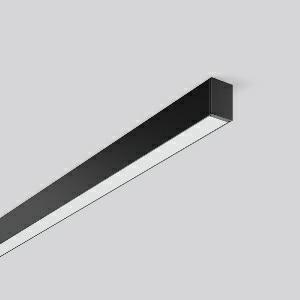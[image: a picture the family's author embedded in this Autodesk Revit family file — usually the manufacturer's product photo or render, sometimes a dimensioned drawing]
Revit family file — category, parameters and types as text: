
# Revit family: less_is_more_27_312198_003_1_fe82
name_source: partatom
category: Lighting Fixtures
units: mm (PartAtom-declared; Revit-internal decimal feet)

## family parameters
Cut with Voids When Loaded = No
Host = Face
Light Source = No
Part Type = Normal
Room Calculation Point = No
Round Connector Dimension = Use Diameter
Shared = No

## types (1)
- LESS IS MORE 27 (1 x LED Modul 840, 1900 lm, 4000)
    Apparent Load = 31 VA
    CIE Flux Codes = 48 79 96 100 100
    Color Rendering = 80
    Color Temperature = 4000
    Default Elevation = 1800 mm
    Description = Series: LESS IS MORE 27
Ceiling and wall luminaire with slim design. Housing: extruded aluminium profile, powder-coated. End cap aluminium powder-coated. Diffuser made of non-yellowing plastic (PMMA), opal. Suitable for Ceiling mounting, Wall (surface). External driver with connecting cable. 
Colour: deep black, matt (RAL 9005)
Length: 1212 mm
Width: 28 mm
Height: 38 mm
Lamp: LED
Socket: without socket
Colour temperature: 4000K
Colour rendering index (CRI): 82
System power: 31 W
Rated luminous flux: 1900 lm
Luminous efficiency: 61 lm/W
Control gear: Regulated power supply
Protection class: II
Type of protection: IP 20
    Height = 38 mm
    Lamp = 1 x LED Modul 840
    Lamp Light Flux = 1900 lm
    Lamp count = 1
    Length = 1212 mm
    Lifetime = 50000 h
    Luminous efficacy = 61 lm/W
    Manufacturer = RZB
    ModVariant = No
    Model = 312198.003.1
    Mounting Place = Ceiling, Wall
    Mounting Type = Surface mounted
    Number of Poles = 1
    OnlyDefault = Yes
    Power Factor = 1
    Product Name = LESS IS MORE 27
    Product group = Surface mounted LED linear luminaires
    ProductGroupID = 307
    Protection Class = Protection class II
    Protection Degree = IP 20
    RLX_Detail_Level = 1
    RLX_Emergency_Light_Flux = 0 lm
    RLX_Emergency_Type = 0
    RLX_Emergency_Type_DB = No
    RlxData = <blob elided: 28685 chars, md5=6dc0d3b8>
    Socket = socket
    Standby Power = 0 W
    System Light Flux = 1900 lm
    System Power = 31 W
    Type Comments = Product without accessories
    Type Image = 312196.003.jpg
    URL = http://relux.com
    VarID = ---
    Voltage = 230 V
    Voltage Range = 220-240 V
    Weight = 0.00 kg
    Width = 28 mm

## geometry (parser evidence)
native form markers: Blend x4, Sweep x12
no freeform markers — native parametric forms only
